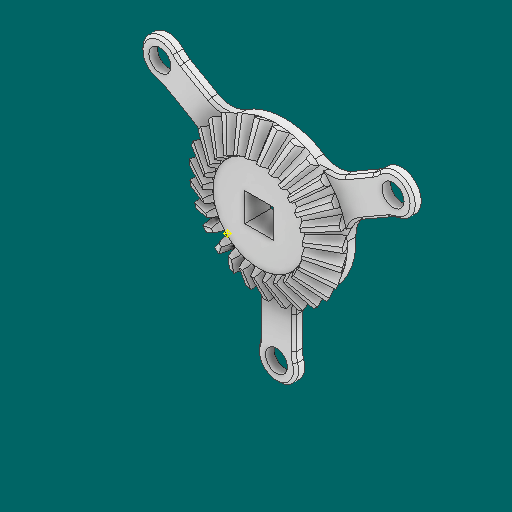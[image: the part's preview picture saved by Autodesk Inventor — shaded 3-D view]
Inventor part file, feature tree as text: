
AUTODESK INVENTOR PART (.ipt)
format: ipt  version: 2023.1 (Build 271208000, 208)  size: 804,864 bytes
history: native  units: in
note: dims shown in document units (in); Inventor stores cm internally (conversion verified against a paired STEP export)
features: other x30, sketch x3
ambient origin geometry x8: Origin, YZ Plane, XZ Plane, XY Plane, X Axis, Y Axis, Z Axis, Center Point
bodies: Solid1 (feature_tree)
feature tree (33):
  other  "Bevel Gear21_MIR.ipt"
  other  "Solid1::Bevel Gear21_MIR.ipt"
  other  "TaggingFeature1"
  other  "Teeth Body Sketch"
  other  "Start Sketch"
  other  "End Sketch"
  other  "End Sketch Right"
  other  "End Sketch Left"
  other  "Body Sketch"
  sketch  "Sketch6"  dims[d0=0.3937in]
  sketch  "Sketch8"  dims[d48=0.0in]
  sketch  "Sketch9"  dims[d49=0.0in d50=90.0deg d52=0.0in d53=0.0in d54=0.0in]
  other  "3D Sketch Right"
  other  "3D Sketch Left"
  other  "Mesh Plane"
  other  "Top Plane"
  other  "Mesh Plane2"
  other  "Tooth Plane"
  other  "End Plane"
  other  "End Plane Right"
  other  "End Plane Left"
  other  "Z Axis_1"
  other  "Top Point"
  other  "Start Point"
  other  "End Point"
  other  "Srf1"
  other  "Srf1::Derived"
  other  "Start plane iMate"
  other  "Mesh iMate2"
  other  "Axis Angle iMate"
  other  "Axis iMate"
  other  "Mesh iMate"
  other  "Intersection iMate"
